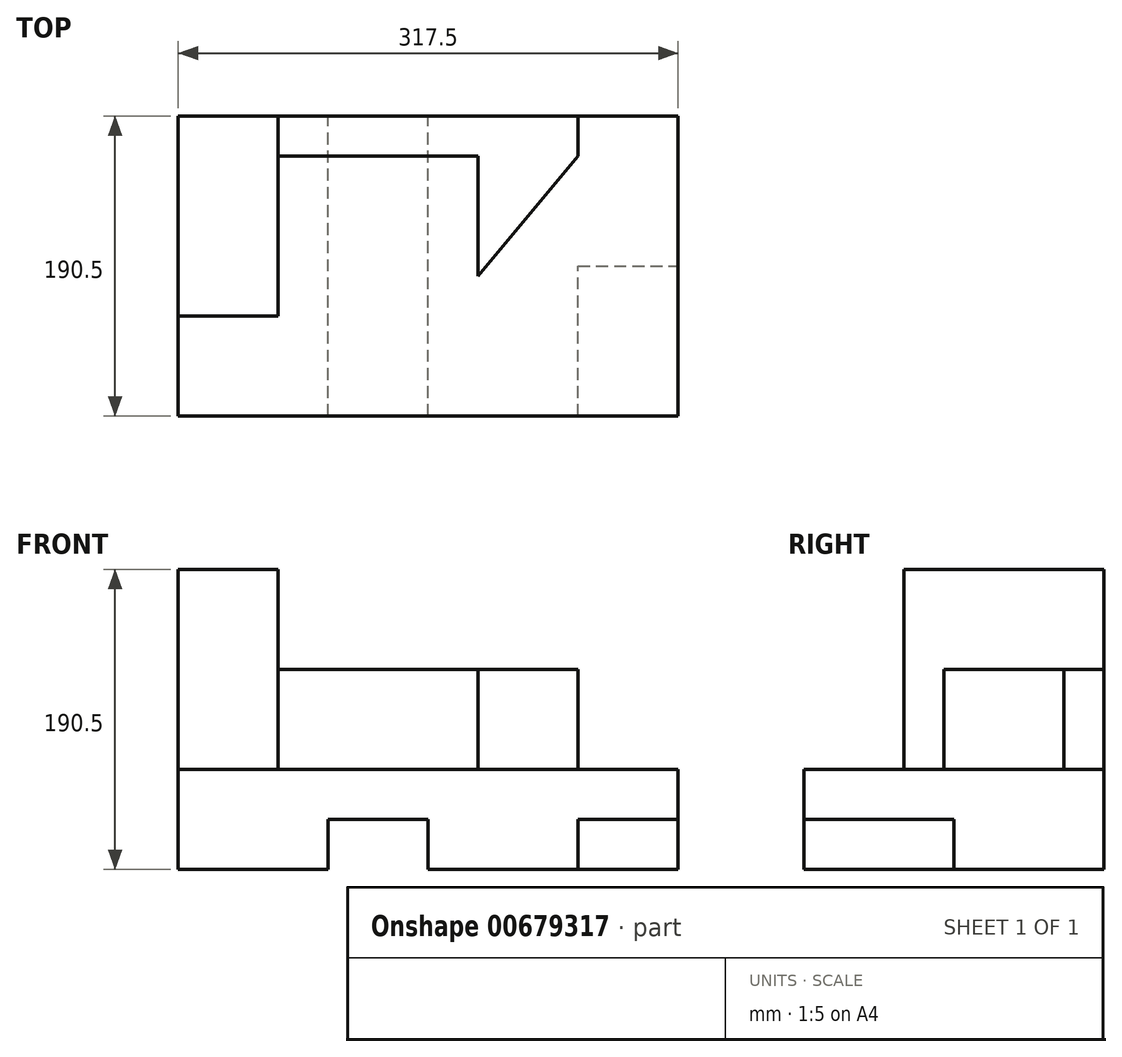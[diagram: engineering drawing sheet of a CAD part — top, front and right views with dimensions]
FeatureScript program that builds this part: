
annotation { "Feature Type Name" : "Feature", "Feature Type Description" : "" }
export const myFeature = defineFeature(function(context is Context, id is Id, definition is map)
    precondition{}
    {
        {
            var Q0;
            Q0=qCreatedBy(makeId("Front.planeOp"),FACE);
            var sketch = newSketch(context, id + "F0", { "sketchPlane" : qUnion([Q0])});
            skLineSegment(sketch, "E0", {"start": v(0, 0) * mm, "end": v(95.25, 0) * mm});
            skLineSegment(sketch, "E1", {"start": v(95.25, 0) * mm, "end": v(95.25, 31.75) * mm});
            skLineSegment(sketch, "E2", {"start": v(95.25, 31.75) * mm, "end": v(158.75, 31.75) * mm});
            skLineSegment(sketch, "E3", {"start": v(158.75, 31.75) * mm, "end": v(158.75, 0) * mm});
            skLineSegment(sketch, "E4", {"start": v(158.75, 0) * mm, "end": v(317.5, 0) * mm});
            skLineSegment(sketch, "E5", {"start": v(317.5, 0) * mm, "end": v(317.5, 63.5) * mm});
            skLineSegment(sketch, "E6", {"start": v(317.5, 63.5) * mm, "end": v(254, 63.5) * mm});
            skLineSegment(sketch, "E7", {"start": v(254, 63.5) * mm, "end": v(254, 127) * mm});
            skLineSegment(sketch, "E8", {"start": v(254, 127) * mm, "end": v(63.5, 127) * mm});
            skLineSegment(sketch, "E9", {"start": v(63.5, 127) * mm, "end": v(63.5, 190.5) * mm});
            skLineSegment(sketch, "E10", {"start": v(63.5, 190.5) * mm, "end": v(0, 190.5) * mm});
            skLineSegment(sketch, "E11", {"start": v(0, 190.5) * mm, "end": v(0, 0) * mm});
            skSolve(sketch);
        }
        {
            var Q0;
            Q0=makeQuery(id+"F0.imprint","IMPRINT",FACE,{"disambiguationData":[TD([[makeQuery(id+"F0.imprint","IMPRINT",EDGE,{"derivedFrom":sQuery(id+"F0.wireOp",EDGE,"E0")}),1.0]])]});
            extrude(context, id + "F1", {"entities" : qUnion([Q0]), "depth" : 25.4 * mm, "offsetDistance" : 25.4 * mm});
        }
        {
            var Q0;
            Q0=makeQuery(id+"F1.opExtrude","CAP_FACE",FACE,{"disambiguationData":[OSD([sQuery(id+"F0.wireOp",EDGE,"E0"),sQuery(id+"F0.wireOp",EDGE,"E1"),sQuery(id+"F0.wireOp",EDGE,"E2"),sQuery(id+"F0.wireOp",EDGE,"E3"),sQuery(id+"F0.wireOp",EDGE,"E4"),sQuery(id+"F0.wireOp",EDGE,"E5"),sQuery(id+"F0.wireOp",EDGE,"E6"),sQuery(id+"F0.wireOp",EDGE,"E7"),sQuery(id+"F0.wireOp",EDGE,"E8"),sQuery(id+"F0.wireOp",EDGE,"E9"),sQuery(id+"F0.wireOp",EDGE,"E10"),sQuery(id+"F0.wireOp",EDGE,"E11")])],"isStart":false});
            var sketch = newSketch(context, id + "F2", { "sketchPlane" : qUnion([Q0])});
            skLineSegment(sketch, "E12", {"start": v(254, 63.5) * mm, "end": v(0, 63.5) * mm});
            skLineSegment(sketch, "E13", {"start": v(95.25, 31.75) * mm, "end": v(0, 31.75) * mm});
            skLineSegment(sketch, "E14", {"start": v(158.75, 31.75) * mm, "end": v(317.5, 31.75) * mm});
            skLineSegment(sketch, "E15", {"start": v(254, 31.75) * mm, "end": v(254, 0) * mm});
            skSolve(sketch);
        }
        {
            var Q0;
            {var subQ2=sQuery(id+"F2.wireOp",EDGE,"E12");Q0=makeQuery(id+"F2.imprint","IMPRINT",FACE,{"disambiguationData":[TD([[makeQuery(id+"F2.imprint","IMPRINT",EDGE,{"derivedFrom":subQ2}),1.0]])]});}
            var Q1;
            {var subQ0=sQuery(id+"F2.wireOp",EDGE,"E13");Q1=makeQuery(id+"F2.imprint","IMPRINT",FACE,{"disambiguationData":[TD([[makeQuery(id+"F2.imprint","IMPRINT",EDGE,{"derivedFrom":subQ0}),1.0]])]});}
            var Q2;
            {var subQ2=sQuery(id+"F2.wireOp",EDGE,"E15");Q2=makeQuery(id+"F2.imprint","IMPRINT",FACE,{"disambiguationData":[TD([[makeQuery(id+"F2.imprint","IMPRINT",EDGE,{"derivedFrom":subQ2}),-1.0]])]});}
            extrude(context, id + "F3", {"entities" : qUnion([Q0, Q1, Q2]), "operationType" : NewBodyOperationType.ADD, "depth" : 165.1 * mm, "offsetDistance" : 25.4 * mm});
        }
        {
            var Q0;
            {var subQ0=sQuery(id+"F0.wireOp",EDGE,"E5");var subQ1=sQuery(id+"F0.wireOp",EDGE,"E4");Q0=makeQuery(id+"F3.boolean.opBoolean","SPLIT",FACE,{"disambiguationData":[TD([makeQuery(id+"F1.opExtrude","SWEPT_FACE",FACE,{"disambiguationData":[OSD([subQ1])]})])],"derivedFrom":makeQuery(id+"F1.opExtrude","CAP_FACE",FACE,{"disambiguationData":[OSD([sQuery(id+"F0.wireOp",EDGE,"E0"),sQuery(id+"F0.wireOp",EDGE,"E1"),sQuery(id+"F0.wireOp",EDGE,"E2"),sQuery(id+"F0.wireOp",EDGE,"E3"),subQ1,subQ0,sQuery(id+"F0.wireOp",EDGE,"E6"),sQuery(id+"F0.wireOp",EDGE,"E7"),sQuery(id+"F0.wireOp",EDGE,"E8"),sQuery(id+"F0.wireOp",EDGE,"E9"),sQuery(id+"F0.wireOp",EDGE,"E10"),sQuery(id+"F0.wireOp",EDGE,"E11")])],"isStart":false})});}
            extrude(context, id + "F4", {"entities" : qUnion([Q0]), "operationType" : NewBodyOperationType.ADD, "depth" : 69.85 * mm, "offsetDistance" : 25.4 * mm});
        }
        {
            var Q0;
            {var subQ0=sQuery(id+"F0.wireOp",EDGE,"E6");Q0=makeQuery(id+"F3.boolean.opBoolean","MERGE",FACE,{"derivedFrom":[makeQuery(id+"F1.opExtrude","SWEPT_FACE",FACE,{"disambiguationData":[OSD([subQ0])]}),makeQuery(id+"F3.opExtrude","SWEPT_FACE",FACE,{"disambiguationData":[OSD([subQ0,sQuery(id+"F2.wireOp",EDGE,"E12")])]})]});}
            var sketch = newSketch(context, id + "F5", { "sketchPlane" : qUnion([Q0])});
            skLineSegment(sketch, "E16", {"start": v(0, -25.4) * mm, "end": v(0, -127) * mm});
            skLineSegment(sketch, "E17", {"start": v(0, -127) * mm, "end": v(63.5, -127) * mm});
            skLineSegment(sketch, "E18", {"start": v(63.5, -127) * mm, "end": v(63.5, -25.4) * mm});
            skSolve(sketch);
        }
        {
            var Q0;
            {var subQ0=sQuery(id+"F5.wireOp",EDGE,"E16");Q0=makeQuery(id+"F5.imprint","IMPRINT",FACE,{"disambiguationData":[TD([[makeQuery(id+"F5.imprint","IMPRINT",EDGE,{"derivedFrom":subQ0}),-1.0]])]});}
            extrude(context, id + "F6", {"entities" : qUnion([Q0]), "operationType" : NewBodyOperationType.ADD, "depth" : 127 * mm, "offsetDistance" : 25.4 * mm});
        }
        {
            var Q0;
            {var subQ0=sQuery(id+"F0.wireOp",EDGE,"E6");Q0=makeQuery(id+"F3.boolean.opBoolean","MERGE",FACE,{"derivedFrom":[makeQuery(id+"F1.opExtrude","SWEPT_FACE",FACE,{"disambiguationData":[OSD([subQ0])]}),makeQuery(id+"F3.opExtrude","SWEPT_FACE",FACE,{"disambiguationData":[OSD([subQ0,sQuery(id+"F2.wireOp",EDGE,"E12")])]})]});}
            var sketch = newSketch(context, id + "F7", { "sketchPlane" : qUnion([Q0])});
            skLineSegment(sketch, "E19", {"start": v(63.5, -101.6) * mm, "end": v(127, -101.6) * mm});
            skLineSegment(sketch, "E20", {"start": v(127, -101.6) * mm, "end": v(127, -25.4) * mm});
            skLineSegment(sketch, "E21", {"start": v(190.5, -25.4) * mm, "end": v(190.5, -101.6) * mm});
            skLineSegment(sketch, "E22", {"start": v(190.5, -101.6) * mm, "end": v(254, -25.4) * mm});
            skSolve(sketch);
        }
        {
            var Q0;
            {var subQ0=sQuery(id+"F7.wireOp",EDGE,"E19");Q0=makeQuery(id+"F7.imprint","IMPRINT",FACE,{"disambiguationData":[TD([[makeQuery(id+"F7.imprint","IMPRINT",EDGE,{"derivedFrom":subQ0}),1.0]])]});}
            var sketch = newSketch(context, id + "F8", { "sketchPlane" : qUnion([Q0])});
            skSolve(sketch);
        }
        {
            var Q0;
            {var subQ0=sQuery(id+"F7.wireOp",EDGE,"E19");Q0=makeQuery(id+"F8.imprint","IMPRINT",FACE,{"disambiguationData":[TD([[makeQuery(id+"F8.imprint","IMPRINT",EDGE,{"derivedFrom":makeQuery(id+"F7.imprint","IMPRINT",EDGE,{"derivedFrom":subQ0})}),1.0]])]});}
            var Q1;
            {var subQ0=sQuery(id+"F7.wireOp",EDGE,"E21");Q1=makeQuery(id+"F7.imprint","IMPRINT",FACE,{"disambiguationData":[TD([[makeQuery(id+"F7.imprint","IMPRINT",EDGE,{"derivedFrom":subQ0}),1.0]])]});}
            extrude(context, id + "F9", {"entities" : qUnion([Q0, Q1]), "operationType" : NewBodyOperationType.ADD, "depth" : 63.5 * mm, "offsetDistance" : 25.4 * mm});
        }
    });
